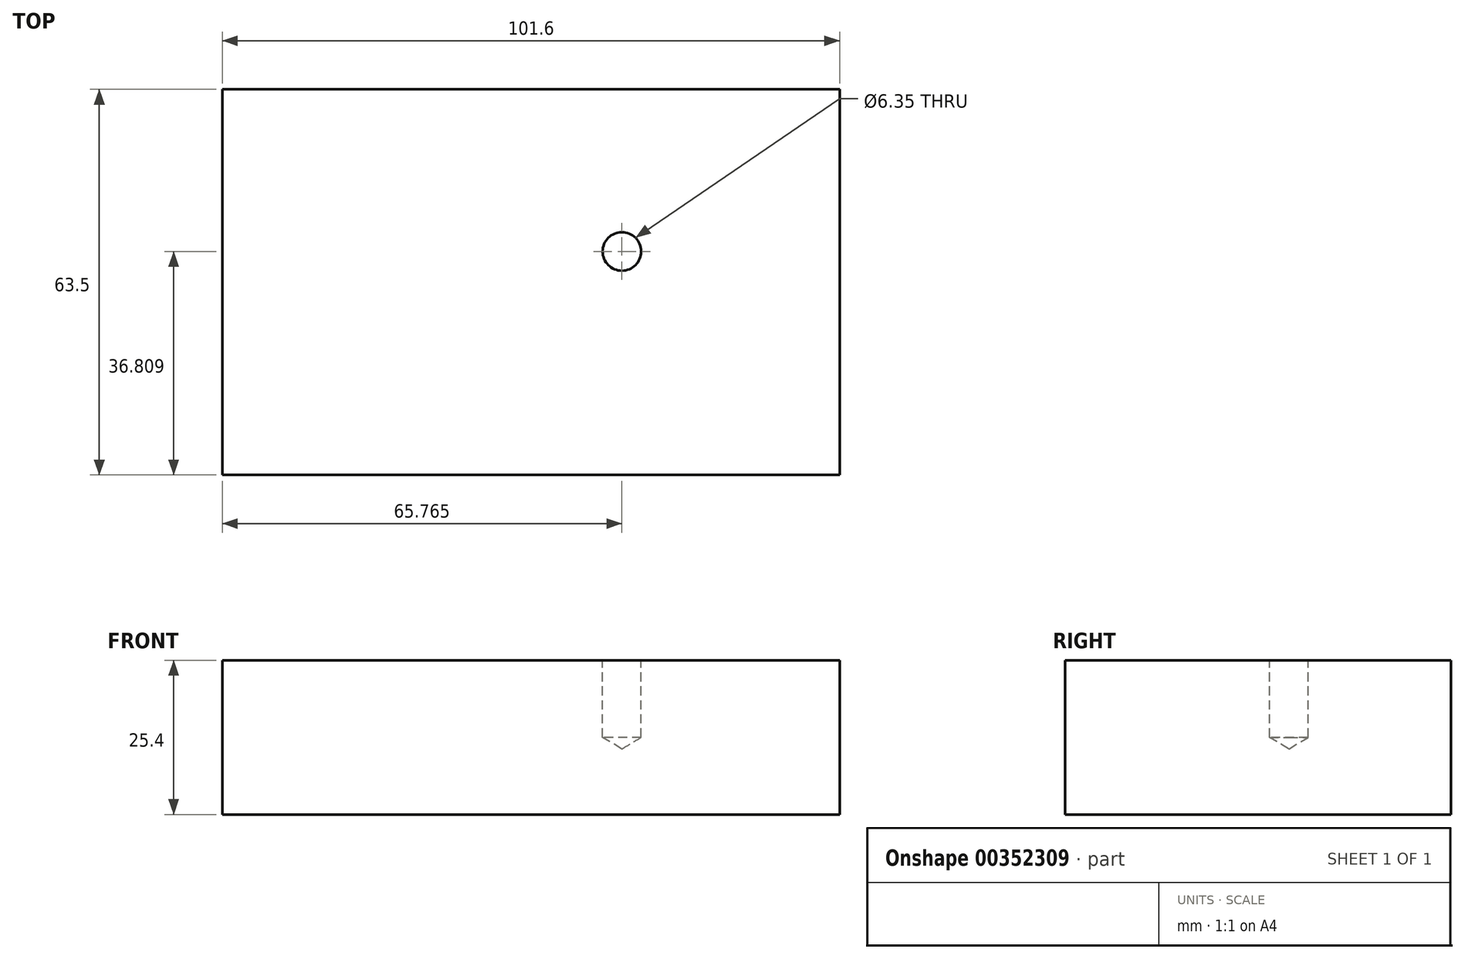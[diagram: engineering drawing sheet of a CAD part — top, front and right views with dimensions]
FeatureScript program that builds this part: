
annotation { "Feature Type Name" : "Feature", "Feature Type Description" : "" }
export const myFeature = defineFeature(function(context is Context, id is Id, definition is map)
    precondition{}
    {
        {
            var Q0;
            Q0=qCreatedBy(makeId("Top.planeOp"),FACE);
            var sketch = newSketch(context, id + "F0", { "sketchPlane" : qUnion([Q0])});
            skLineSegment(sketch, "E0.bottom", {"start": v(-54.05, 37.13) * mm, "end": v(47.55, 37.13) * mm});
            skLineSegment(sketch, "E0.top", {"start": v(-54.05, -26.37) * mm, "end": v(47.55, -26.37) * mm});
            skLineSegment(sketch, "E0.left", {"start": v(-54.05, 37.13) * mm, "end": v(-54.05, -26.37) * mm});
            skLineSegment(sketch, "E0.right", {"start": v(47.55, 37.13) * mm, "end": v(47.55, -26.37) * mm});
            skSolve(sketch);
        }
        {
            var Q0;
            Q0 = qSketchRegion(id + "F0", true);
            extrude(context, id + "F1", {"entities" : qUnion([Q0]), "endBound" : BoundingType.SYMMETRIC, "depth" : 25.4 * mm});
        }
        {
            var Q0;
            Q0=makeQuery(id+"F1.opExtrude","CAP_FACE",FACE,{"disambiguationData":[OSD([sQuery(id+"F0.wireOp",EDGE,"E0.bottom"),sQuery(id+"F0.wireOp",EDGE,"E0.top"),sQuery(id+"F0.wireOp",EDGE,"E0.left"),sQuery(id+"F0.wireOp",EDGE,"E0.right")])],"isStart":false});
            var sketch = newSketch(context, id + "F2", { "sketchPlane" : qUnion([Q0])});
            skPoint(sketch, "E1", {"position": v(11.71, 10.44) * mm});
            skSolve(sketch);
        }
        {
            var Q0;
            Q0=sQuery(id+"F2.wireOp",VERTEX,"E1");
            var Q1;
            Q1=makeQuery(id+"F1.opExtrude","SWEPT_BODY",BODY,{"disambiguationData":[OSD([sQuery(id+"F0.wireOp",EDGE,"E0.bottom"),sQuery(id+"F0.wireOp",EDGE,"E0.top"),sQuery(id+"F0.wireOp",EDGE,"E0.left"),sQuery(id+"F0.wireOp",EDGE,"E0.right")])]});
            hole(context, id + "F3", {"style" : HoleStyle.SIMPLE, "endStyle" : HoleEndStyle.BLIND, "holeDiameter" : 6.35 * mm, "holeDepth" : 12.7 * mm, "isTappedThrough" : true, "tappedDepth" : 12.7 * mm, "tapClearance" : 3, "locations" : qUnion([Q0]), "scope" : qUnion([Q1])});
        }
    });
